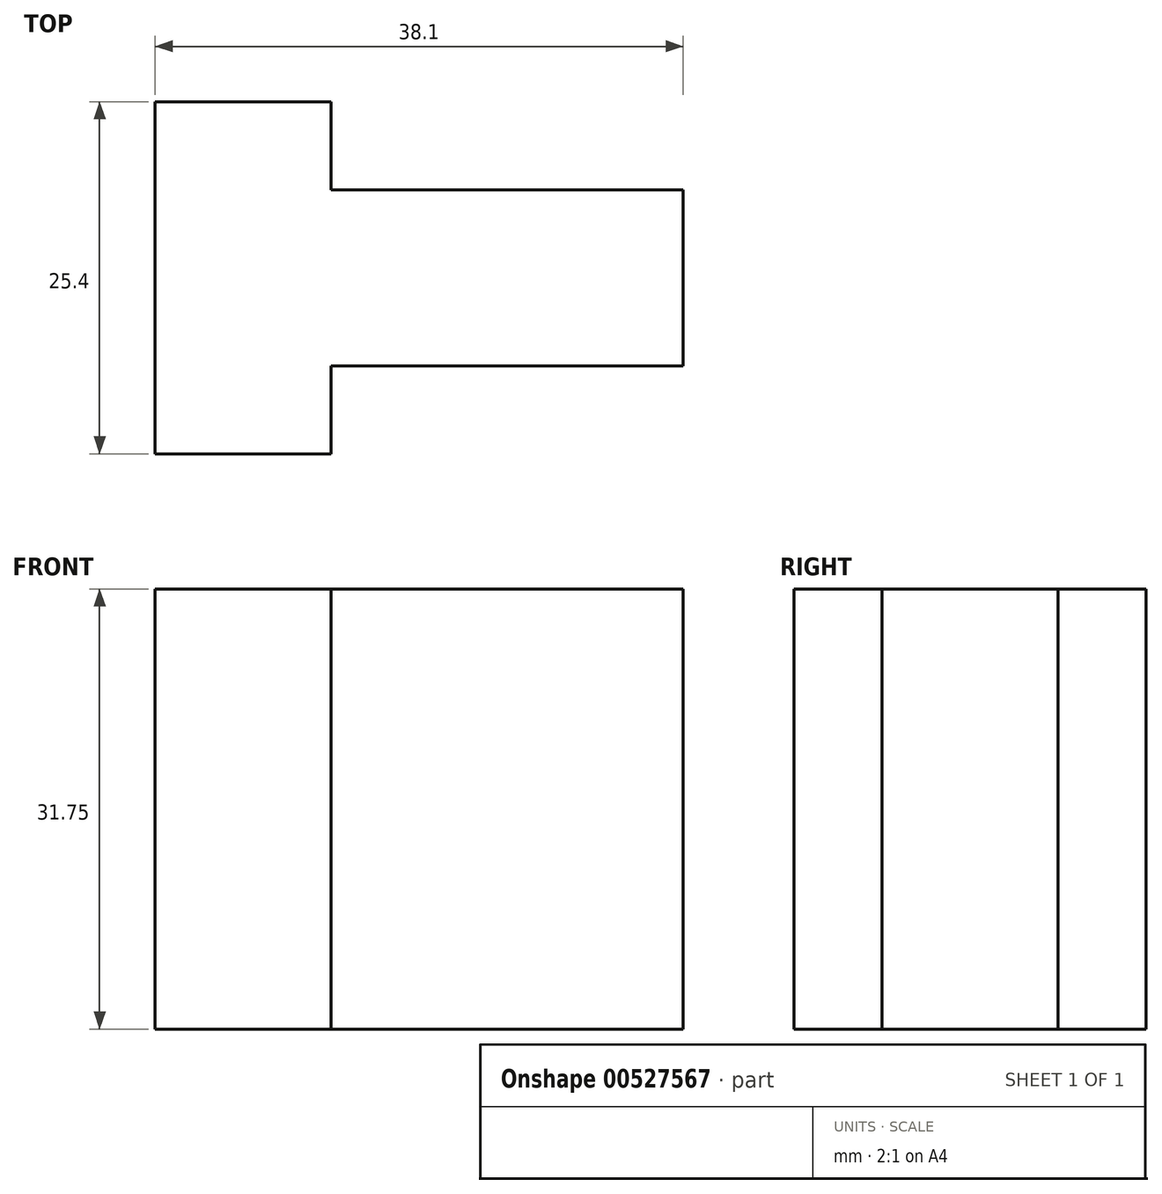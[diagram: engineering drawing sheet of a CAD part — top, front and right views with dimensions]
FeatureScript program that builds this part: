
annotation { "Feature Type Name" : "Feature", "Feature Type Description" : "" }
export const myFeature = defineFeature(function(context is Context, id is Id, definition is map)
    precondition{}
    {
        {
            var Q0;
            Q0=qCreatedBy(makeId("Top.planeOp"),FACE);
            var sketch = newSketch(context, id + "F0", { "sketchPlane" : qUnion([Q0])});
            skLineSegment(sketch, "E0", {"start": v(0, 0) * mm, "end": v(0, 25.4) * mm});
            skLineSegment(sketch, "E1", {"start": v(0, 25.4) * mm, "end": v(12.7, 25.4) * mm});
            skLineSegment(sketch, "E2", {"start": v(12.7, 25.4) * mm, "end": v(12.7, 19.05) * mm});
            skLineSegment(sketch, "E3", {"start": v(12.7, 19.05) * mm, "end": v(38.1, 19.05) * mm});
            skLineSegment(sketch, "E4", {"start": v(38.1, 19.05) * mm, "end": v(38.1, 6.35) * mm});
            skLineSegment(sketch, "E5", {"start": v(38.1, 6.35) * mm, "end": v(12.7, 6.35) * mm});
            skLineSegment(sketch, "E6", {"start": v(12.7, 6.35) * mm, "end": v(12.7, 0) * mm});
            skLineSegment(sketch, "E7", {"start": v(0, 0) * mm, "end": v(12.7, 0) * mm});
            skSolve(sketch);
        }
        {
            var Q0;
            Q0 = qSketchRegion(id + "F0", true);
            var Q1;
            Q1=makeQuery(id+"F0.imprint","IMPRINT",FACE,{"disambiguationData":[TD([[makeQuery(id+"F0.imprint","IMPRINT",EDGE,{"derivedFrom":sQuery(id+"F0.wireOp",EDGE,"E0")}),-1.0]])]});
            extrude(context, id + "F1", {"entities" : qUnion([Q0, Q1]), "depth" : 31.75 * mm, "offsetDistance" : 25.4 * mm});
        }
    });
